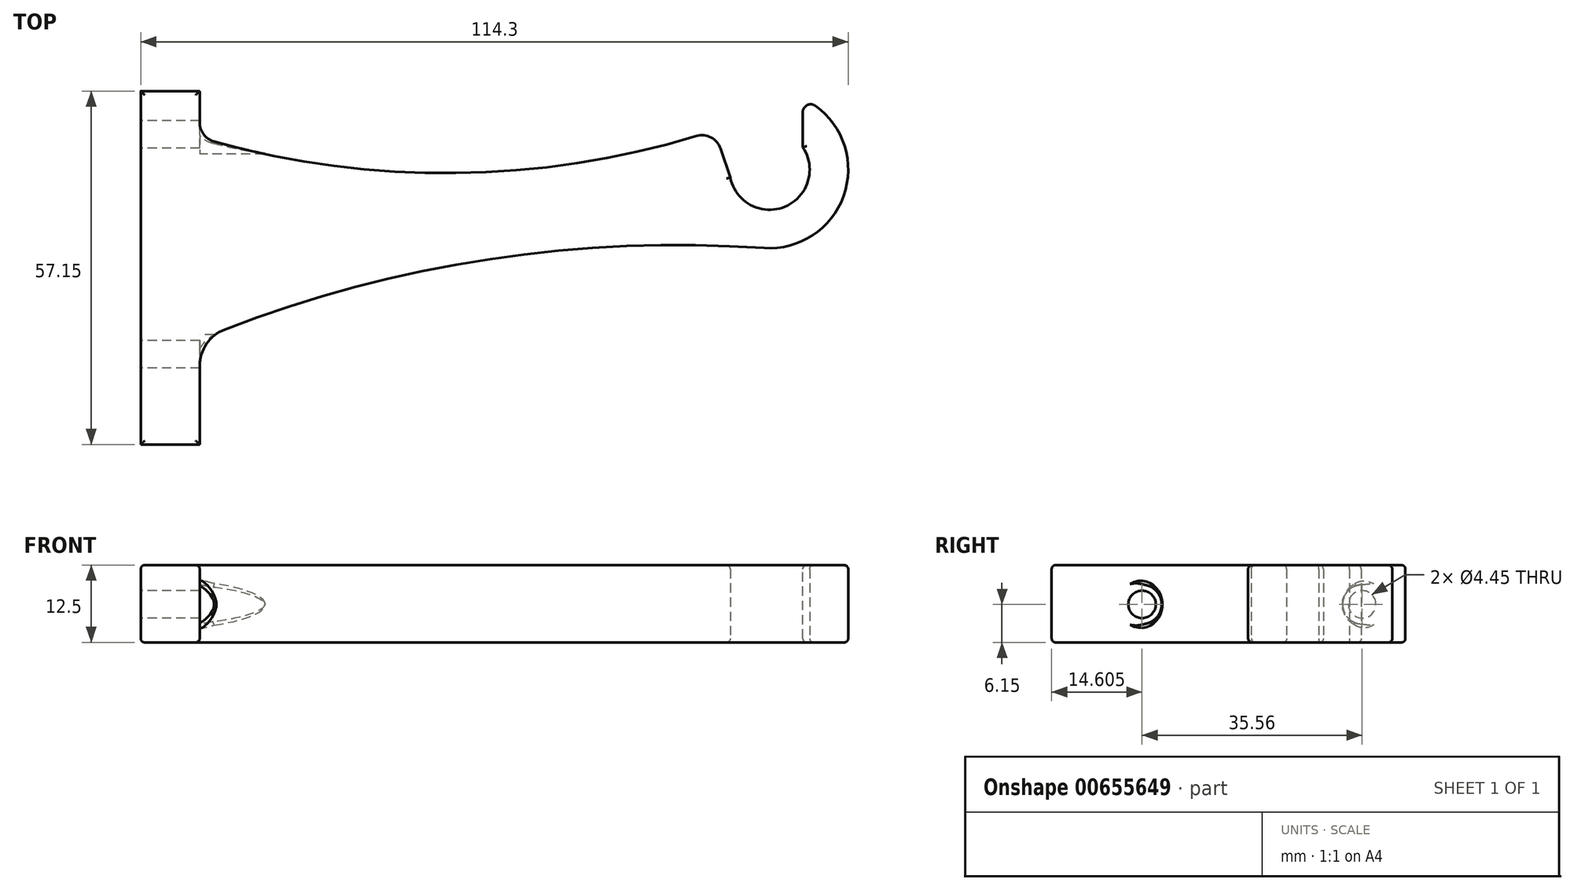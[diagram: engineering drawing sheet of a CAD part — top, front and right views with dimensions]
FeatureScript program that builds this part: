
annotation { "Feature Type Name" : "Feature", "Feature Type Description" : "" }
export const myFeature = defineFeature(function(context is Context, id is Id, definition is map)
    precondition{}
    {
        {
            var Q0;
            Q0=qCreatedBy(makeId("Top.planeOp"),FACE);
            var sketch = newSketch(context, id + "F0", { "sketchPlane" : qUnion([Q0])});
            skArc(sketch, "E0", {"start": v(-6.35, -1.27) * mm, "mid": v(2.5, -5.98) * mm, "end": v(5.37, 3.63) * mm});
            skLineSegment(sketch, "E1", {"start": v(-101.6, 12.7) * mm, "end": v(-101.6, -44.45) * mm});
            skLineSegment(sketch, "E2", {"start": v(-101.6, -44.45) * mm, "end": v(-92.08, -44.45) * mm});
            skLineSegment(sketch, "E3", {"start": v(-92.07, -44.45) * mm, "end": v(-92.07, -31.75) * mm});
            skLineSegment(sketch, "E4", {"start": v(-101.6, 12.7) * mm, "end": v(-92.07, 12.7) * mm});
            skLineSegment(sketch, "E5", {"start": v(-92.07, 12.7) * mm, "end": v(-92.07, 7.62) * mm});
            skArc(sketch, "E6", {"start": v(-0.87, -12.67) * mm, "mid": v(-45.16, -14.47) * mm, "end": v(-88.01, -25.83) * mm});
            skArc(sketch, "E7", {"start": v(-89.75, 4.56) * mm, "mid": v(-49.19, -0.52) * mm, "end": v(-8.9, 6.35) * mm});
            skArc(sketch, "E8", {"start": v(-0.87, -12.67) * mm, "mid": v(12.3, -3.17) * mm, "end": v(5.37, 11.51) * mm});
            skPoint(sketch, "E9.orphan", {"position": v(0, 9.6) * mm});
            skPoint(sketch, "E10.visualSharp", {"position": v(-92.08, 5.23) * mm});
            skArc(sketch, "E10.filletArc", {"start": v(-92.08, 7.62) * mm, "mid": v(-91.43, 5.7) * mm, "end": v(-89.75, 4.56) * mm});
            skPoint(sketch, "E11.visualSharp", {"position": v(-92.07, -27.45) * mm});
            skArc(sketch, "E11.filletArc", {"start": v(-88.01, -25.83) * mm, "mid": v(-90.96, -28.16) * mm, "end": v(-92.08, -31.75) * mm});
            skLineSegment(sketch, "E12", {"start": v(5.37, 3.63) * mm, "end": v(5.37, 11.51) * mm});
            skLineSegment(sketch, "E13", {"start": v(-6.35, -1.27) * mm, "end": v(-8.9, 6.35) * mm});
            skSolve(sketch);
        }
        {
            var Q0;
            Q0 = qSketchRegion(id + "F0", true);
            extrude(context, id + "F1", {"entities" : qUnion([Q0]), "depth" : 12.5 * mm, "offsetDistance" : 25.4 * mm});
        }
        {
            var Q0;
            Q0=makeQuery(id+"F1.opExtrude","CAP_FACE",FACE,{"disambiguationData":[OSD([sQuery(id+"F0.wireOp",EDGE,"E0"),sQuery(id+"F0.wireOp",EDGE,"E1"),sQuery(id+"F0.wireOp",EDGE,"E2"),sQuery(id+"F0.wireOp",EDGE,"E3"),sQuery(id+"F0.wireOp",EDGE,"E4"),sQuery(id+"F0.wireOp",EDGE,"E5"),sQuery(id+"F0.wireOp",EDGE,"E6"),sQuery(id+"F0.wireOp",EDGE,"E7"),sQuery(id+"F0.wireOp",EDGE,"E8"),sQuery(id+"F0.wireOp",EDGE,"E10.filletArc"),sQuery(id+"F0.wireOp",EDGE,"E11.filletArc"),sQuery(id+"F0.wireOp",EDGE,"E12"),sQuery(id+"F0.wireOp",EDGE,"E13")])],"isStart":false});
            fillet(context, id + "F2", {"entities" : qUnion([Q0]), "radius" : 0.64 * mm, "tangentPropagation" : true, "allowEdgeOverflow" : false});
        }
        {
            var Q0;
            Q0=makeQuery(id+"F1.opExtrude","CAP_FACE",FACE,{"disambiguationData":[OSD([sQuery(id+"F0.wireOp",EDGE,"E0"),sQuery(id+"F0.wireOp",EDGE,"E1"),sQuery(id+"F0.wireOp",EDGE,"E2"),sQuery(id+"F0.wireOp",EDGE,"E3"),sQuery(id+"F0.wireOp",EDGE,"E4"),sQuery(id+"F0.wireOp",EDGE,"E5"),sQuery(id+"F0.wireOp",EDGE,"E6"),sQuery(id+"F0.wireOp",EDGE,"E7"),sQuery(id+"F0.wireOp",EDGE,"E8"),sQuery(id+"F0.wireOp",EDGE,"E10.filletArc"),sQuery(id+"F0.wireOp",EDGE,"E11.filletArc"),sQuery(id+"F0.wireOp",EDGE,"E12"),sQuery(id+"F0.wireOp",EDGE,"E13")])],"isStart":true});
            fillet(context, id + "F3", {"entities" : qUnion([Q0]), "radius" : 0.64 * mm, "tangentPropagation" : true, "allowEdgeOverflow" : false});
        }
        {
            var Q0;
            Q0=makeQuery(id+"F1.opExtrude","SWEPT_EDGE",EDGE,{"disambiguationData":[OSD([sQuery(id+"F0.wireOp",EDGE,"E7"),sQuery(id+"F0.wireOp",EDGE,"E13")])]});
            fillet(context, id + "F4", {"entities" : qUnion([Q0]), "radius" : 3.17 * mm, "tangentPropagation" : true, "allowEdgeOverflow" : false});
        }
        {
            var Q0;
            Q0=makeQuery(id+"F1.opExtrude","SWEPT_EDGE",EDGE,{"disambiguationData":[OSD([sQuery(id+"F0.wireOp",EDGE,"E8"),sQuery(id+"F0.wireOp",EDGE,"E12")])]});
            fillet(context, id + "F5", {"entities" : qUnion([Q0]), "radius" : 1.27 * mm, "tangentPropagation" : true, "allowEdgeOverflow" : false});
        }
        {
            var Q0;
            Q0=makeQuery(id+"F1.opExtrude","SWEPT_FACE",FACE,{"disambiguationData":[OSD([sQuery(id+"F0.wireOp",EDGE,"E3")])]});
            var sketch = newSketch(context, id + "F6", { "sketchPlane" : qUnion([Q0])});
            skCircle(sketch, "E14", {"center": v(-29.84, 6.15) * mm, "radius": 2.22 * mm});
            skSolve(sketch);
        }
        {
            var Q0;
            Q0 = qSketchRegion(id + "F6", true);
            extrude(context, id + "F7", {"entities" : qUnion([Q0]), "operationType" : NewBodyOperationType.REMOVE, "depth" : 25.4 * mm, "offsetDistance" : 25.4 * mm, "hasSecondDirection" : true, "secondDirectionOppositeDirection" : true, "secondDirectionDepth" : 25.4 * mm});
        }
        {
            var Q0;
            Q0=makeQuery(id+"F1.opExtrude","SWEPT_FACE",FACE,{"disambiguationData":[OSD([sQuery(id+"F0.wireOp",EDGE,"E3")])]});
            var sketch = newSketch(context, id + "F8", { "sketchPlane" : qUnion([Q0])});
            skCircle(sketch, "E15", {"center": v(-29.84, 6.15) * mm, "radius": 3.18 * mm});
            skSolve(sketch);
        }
        {
            var Q0;
            Q0 = qSketchRegion(id + "F8", true);
            extrude(context, id + "F9", {"entities" : qUnion([Q0]), "operationType" : NewBodyOperationType.REMOVE, "depth" : 25.4 * mm, "offsetDistance" : 25.4 * mm});
        }
        {
            var Q0;
            Q0=makeQuery(id+"F1.opExtrude","SWEPT_FACE",FACE,{"disambiguationData":[OSD([sQuery(id+"F0.wireOp",EDGE,"E5")])]});
            var sketch = newSketch(context, id + "F10", { "sketchPlane" : qUnion([Q0])});
            skCircle(sketch, "E16", {"center": v(5.72, 6.15) * mm, "radius": 2.22 * mm});
            skSolve(sketch);
        }
        {
            var Q0;
            Q0 = qSketchRegion(id + "F10", true);
            extrude(context, id + "F11", {"entities" : qUnion([Q0]), "operationType" : NewBodyOperationType.REMOVE, "depth" : 9.52 * mm, "offsetDistance" : 25.4 * mm, "hasSecondDirection" : true, "secondDirectionOppositeDirection" : true, "secondDirectionDepth" : 25.4 * mm});
        }
        {
            var Q0;
            Q0=makeQuery(id+"F1.opExtrude","SWEPT_FACE",FACE,{"disambiguationData":[OSD([sQuery(id+"F0.wireOp",EDGE,"E5")])]});
            var sketch = newSketch(context, id + "F12", { "sketchPlane" : qUnion([Q0])});
            skCircle(sketch, "E17", {"center": v(5.72, 6.15) * mm, "radius": 3.18 * mm});
            skSolve(sketch);
        }
        {
            var Q0;
            Q0 = qSketchRegion(id + "F12", true);
            extrude(context, id + "F13", {"entities" : qUnion([Q0]), "operationType" : NewBodyOperationType.REMOVE, "depth" : 9.52 * mm, "offsetDistance" : 25.4 * mm});
        }
        {
            var Q0;
            Q0=makeQuery(id+"F13.boolean.opBoolean","INTERSECT",EDGE,{"disambiguationData":[OD(1.0)],"derivedFrom":[makeQuery(id+"F1.opExtrude","SWEPT_FACE",FACE,{"disambiguationData":[OSD([sQuery(id+"F0.wireOp",EDGE,"E7")])]}),makeQuery(id+"F13.opExtrude","SWEPT_FACE",FACE,{"disambiguationData":[OSD([sQuery(id+"F12.wireOp",EDGE,"E17")])]})]});
            var Q1;
            Q1=makeQuery(id+"F13.boolean.opBoolean","INTERSECT",EDGE,{"derivedFrom":[makeQuery(id+"F1.opExtrude","SWEPT_FACE",FACE,{"disambiguationData":[OSD([sQuery(id+"F0.wireOp",EDGE,"E7")])]}),makeQuery(id+"F13.opExtrude","CAP_FACE",FACE,{"disambiguationData":[OSD([sQuery(id+"F12.wireOp",EDGE,"E17")])],"isStart":false})]});
            var Q2;
            Q2=makeQuery(id+"F13.boolean.opBoolean","INTERSECT",EDGE,{"disambiguationData":[OD(0.0)],"derivedFrom":[makeQuery(id+"F1.opExtrude","SWEPT_FACE",FACE,{"disambiguationData":[OSD([sQuery(id+"F0.wireOp",EDGE,"E7")])]}),makeQuery(id+"F13.opExtrude","SWEPT_FACE",FACE,{"disambiguationData":[OSD([sQuery(id+"F12.wireOp",EDGE,"E17")])]})]});
            var Q3;
            Q3=makeQuery(id+"F9.boolean.opBoolean","INTERSECT",EDGE,{"derivedFrom":[makeQuery(id+"F1.opExtrude","SWEPT_FACE",FACE,{"disambiguationData":[OSD([sQuery(id+"F0.wireOp",EDGE,"E11.filletArc")])]}),makeQuery(id+"F9.opExtrude","SWEPT_FACE",FACE,{"disambiguationData":[OSD([sQuery(id+"F8.wireOp",EDGE,"E15")])]})]});
            fillet(context, id + "F14", {"entities" : qUnion([Q0, Q1, Q2, Q3]), "radius" : 0.64 * mm, "tangentPropagation" : true, "allowEdgeOverflow" : false});
        }
    });
